# Revit family: Roof-Deck_Precast
name_source: partatom
category: Structural Framing
revit_build: Autodesk Revit Architecture 2012 (Build: 20110309_2315(x64)
units: mm (PartAtom-declared; Revit-internal decimal feet)

## types (3) — shared parameters
Assembly Code = B1020342
Compressive Strength = 5000.00 psi
Concrete Type = ARCAT - Concrete - Precast_5000psi
Construction Details = http://www.arcat.com
Expected Lifespan (Years) = 50
Green Building-LEED = http://www.arcat.com
Keynote = 03410
Manufacturer = Generic
Manufacturer Fax = (203) 939-2444
Manufacturer Website = http://www.arcat.com
Model = Generic
Product Data = http://www.arcat.com
Product Properties = http://www.arcat.com
Span Rating = 26' - 0"
Specification = http://www.arcat.com
Warranty Duration (Years) = 5
zero-valued in all types: Maintenance Schedule (Months)

## per-type parameters (varying)
| type | Depth | Description | Leg Separation | Width |
| 10" Double-T | 0' - 3 1/2" | 10" Wide Precast Double-T Roof Deck | 0' - 3" | 0' - 10" |
| 12" Double-T | 0' - 4" | 12" Wide Precast Double-T Roof Deck | 0' - 3 1/2" | 1' - 0" |
| 18" Double-T | 0' - 6" | 18" Wide Precast Double-T Roof Deck | 0' - 5" | 1' - 6" |

## geometry (parser evidence)
native form markers: Sweep x2
no freeform markers — native parametric forms only
